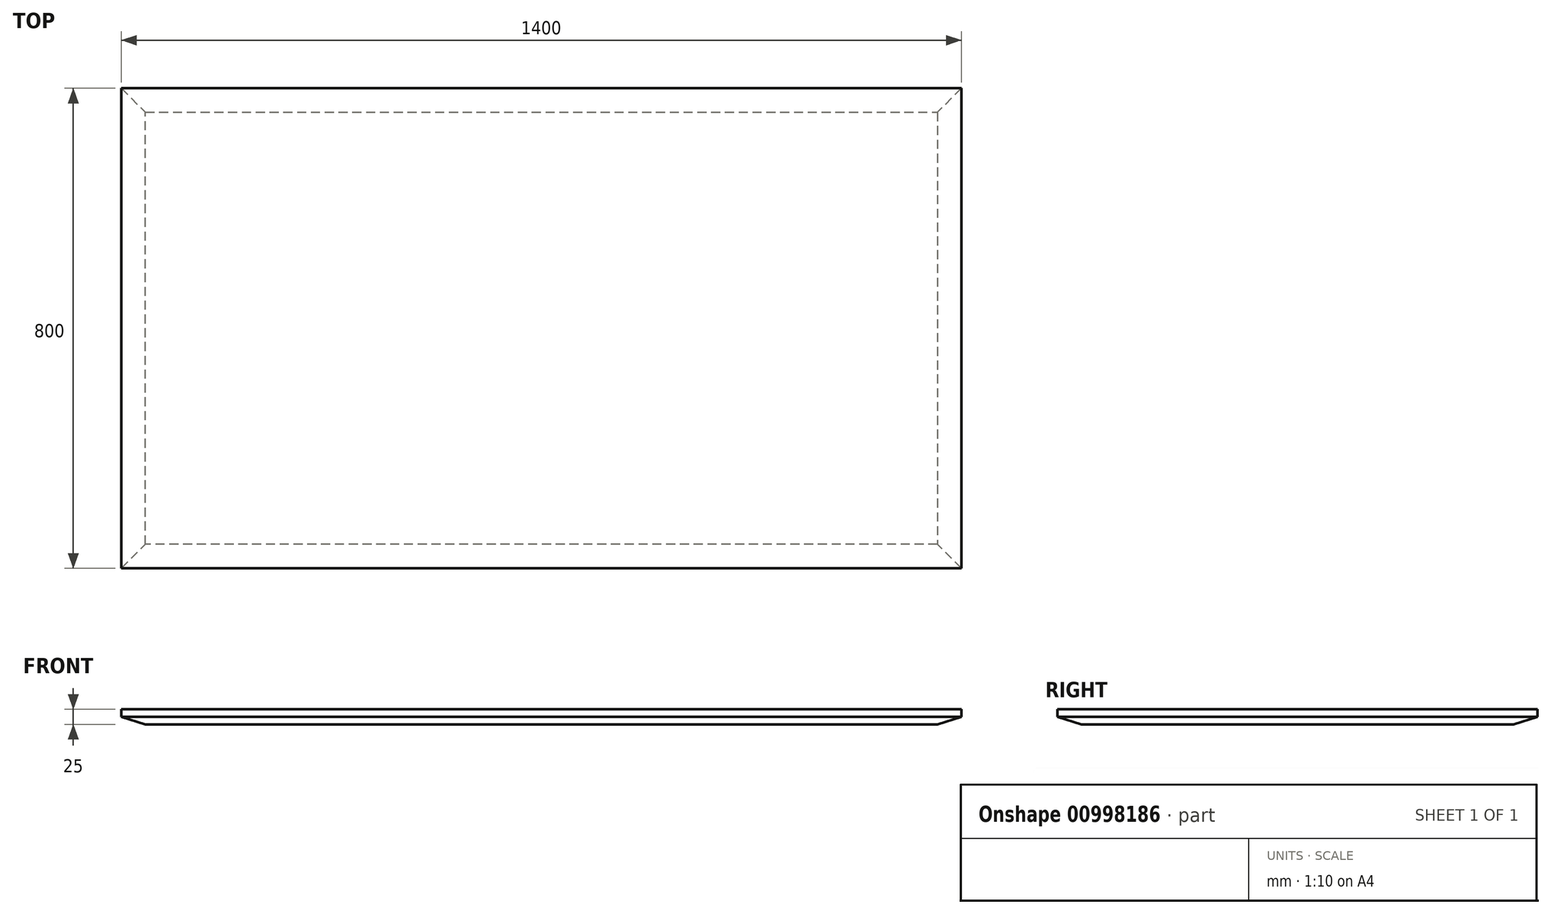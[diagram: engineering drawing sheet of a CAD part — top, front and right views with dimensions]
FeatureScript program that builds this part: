
annotation { "Feature Type Name" : "Feature", "Feature Type Description" : "" }
export const myFeature = defineFeature(function(context is Context, id is Id, definition is map)
    precondition{}
    {
        {
            var Q0;
            Q0=qCreatedBy(makeId("Top.planeOp"),FACE);
            var sketch = newSketch(context, id + "F0", { "sketchPlane" : qUnion([Q0])});
            skLineSegment(sketch, "E0.bottom", {"start": v(0, 0) * mm, "end": v(-1400, 0) * mm});
            skLineSegment(sketch, "E0.top", {"start": v(0, 800) * mm, "end": v(-1400, 800) * mm});
            skLineSegment(sketch, "E0.left", {"start": v(0, 0) * mm, "end": v(0, 800) * mm});
            skLineSegment(sketch, "E0.right", {"start": v(-1400, 0) * mm, "end": v(-1400, 800) * mm});
            skSolve(sketch);
        }
        {
            var Q0;
            Q0 = qSketchRegion(id + "F0", true);
            extrude(context, id + "F1", {"entities" : qUnion([Q0]), "depth" : 25 * mm, "offsetDistance" : 25 * mm});
        }
        {
            var Q0;
            Q0=makeQuery(id+"F1.opExtrude","CAP_FACE",FACE,{"disambiguationData":[OSD([sQuery(id+"F0.wireOp",EDGE,"E0.bottom"),sQuery(id+"F0.wireOp",EDGE,"E0.top"),sQuery(id+"F0.wireOp",EDGE,"E0.left"),sQuery(id+"F0.wireOp",EDGE,"E0.right")])],"isStart":true});
            chamfer(context, id + "F2", {"entities" : qUnion([Q0]), "chamferType" : ChamferType.TWO_OFFSETS, "width1" : 40 * mm, "oppositeDirection" : false, "width2" : 12.5 * mm, "tangentPropagation" : true});
        }
    });
